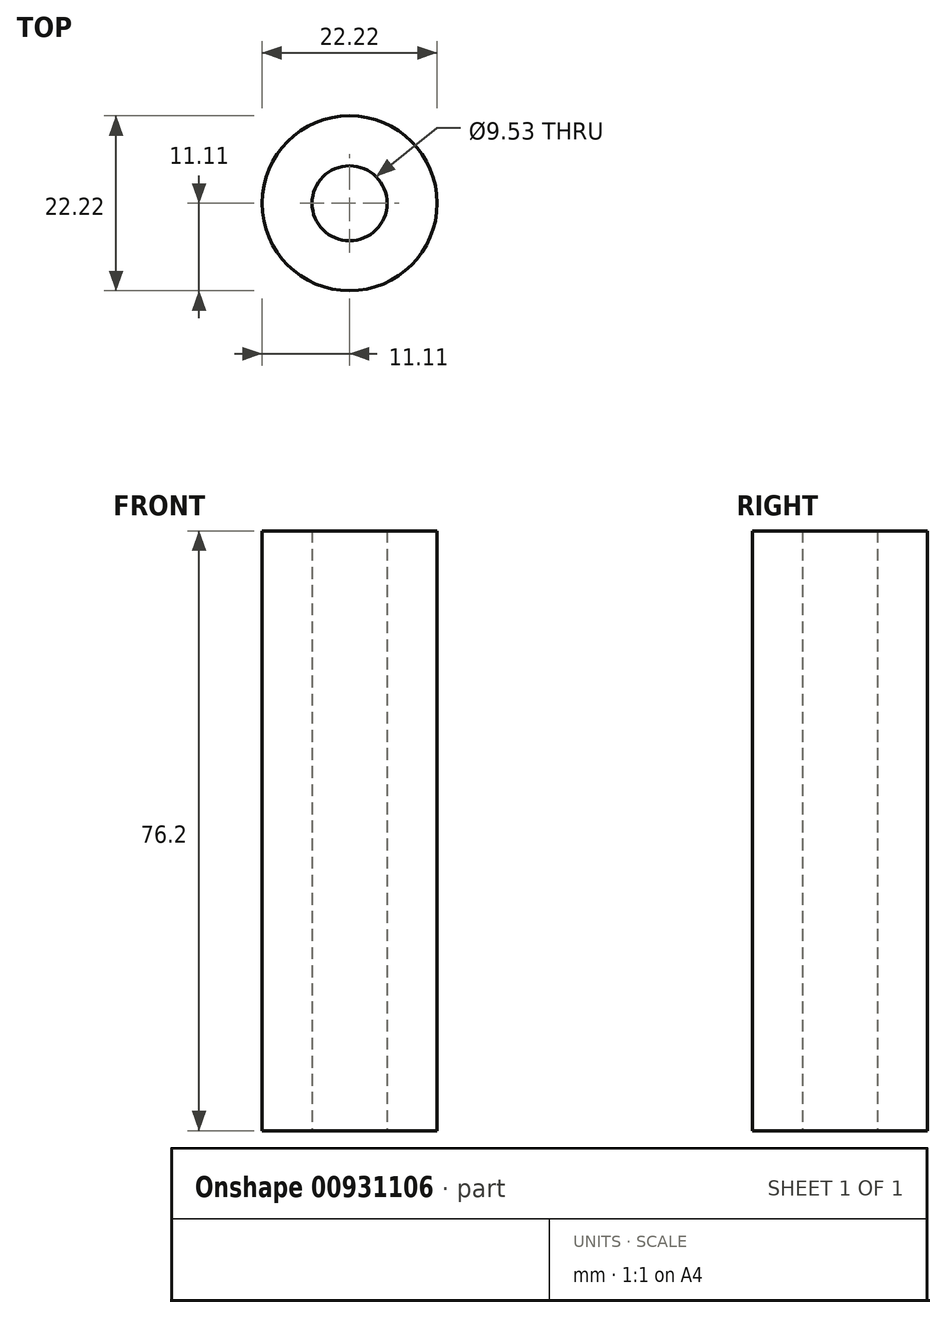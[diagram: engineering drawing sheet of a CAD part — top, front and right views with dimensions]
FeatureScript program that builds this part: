
annotation { "Feature Type Name" : "Feature", "Feature Type Description" : "" }
export const myFeature = defineFeature(function(context is Context, id is Id, definition is map)
    precondition{}
    {
        {
            var Q0;
            Q0=qCreatedBy(makeId("Top.planeOp"),FACE);
            var sketch = newSketch(context, id + "F0", { "sketchPlane" : qUnion([Q0])});
            skCircle(sketch, "E0", {"center": v(0, 0) * mm, "radius": 4.76 * mm});
            skCircle(sketch, "E1", {"center": v(0, 0) * mm, "radius": 11.11 * mm});
            skSolve(sketch);
        }
        {
            var Q0;
            Q0=makeQuery(id+"F0.imprint","IMPRINT",FACE,{"disambiguationData":[TD([[makeQuery(id+"F0.imprint","IMPRINT",EDGE,{"derivedFrom":sQuery(id+"F0.wireOp",EDGE,"E0")}),-1.0]])]});
            extrude(context, id + "F1", {"entities" : qUnion([Q0]), "depth" : 76.2 * mm, "offsetDistance" : 25.4 * mm});
        }
    });
